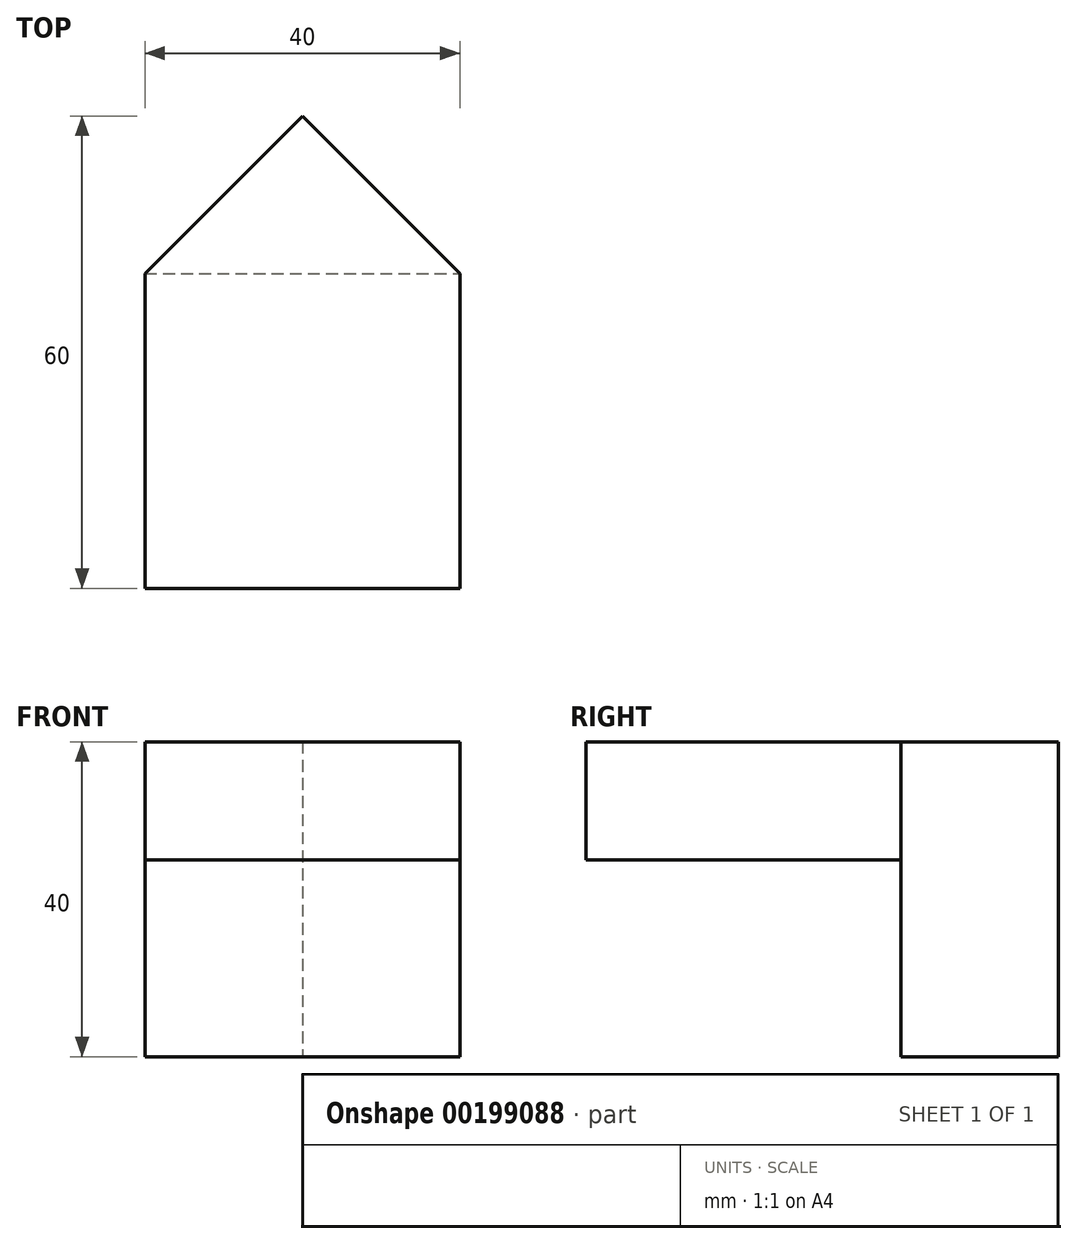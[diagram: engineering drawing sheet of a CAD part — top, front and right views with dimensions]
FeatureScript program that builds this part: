
annotation { "Feature Type Name" : "Feature", "Feature Type Description" : "" }
export const myFeature = defineFeature(function(context is Context, id is Id, definition is map)
    precondition{}
    {
        {
            var Q0;
            Q0=qCreatedBy(makeId("Top.planeOp"),FACE);
            var sketch = newSketch(context, id + "F0", { "sketchPlane" : qUnion([Q0])});
            skLineSegment(sketch, "E0.bottom", {"start": v(0, 0) * mm, "end": v(40, 0) * mm});
            skLineSegment(sketch, "E0.top", {"start": v(0, -40) * mm, "end": v(40, -40) * mm});
            skLineSegment(sketch, "E0.left", {"start": v(0, 0) * mm, "end": v(0, -40) * mm});
            skLineSegment(sketch, "E0.right", {"start": v(40, 0) * mm, "end": v(40, -40) * mm});
            skLineSegment(sketch, "E1", {"start": v(0, 0) * mm, "end": v(20, 20) * mm});
            skLineSegment(sketch, "E2", {"start": v(20, 20) * mm, "end": v(40, 0) * mm});
            skSolve(sketch);
        }
        {
            var Q0;
            Q0 = qSketchRegion(id + "F0", true);
            extrude(context, id + "F1", {"entities" : qUnion([Q0]), "depth" : 40 * mm, "offsetDistance" : 25 * mm});
        }
        {
            var Q0;
            Q0=makeQuery(id+"F0.imprint","IMPRINT",FACE,{"disambiguationData":[TD([[makeQuery(id+"F0.imprint","IMPRINT",EDGE,{"derivedFrom":sQuery(id+"F0.wireOp",EDGE,"E0.bottom")}),-1.0]])]});
            extrude(context, id + "F2", {"entities" : qUnion([Q0]), "operationType" : NewBodyOperationType.REMOVE, "depth" : 25 * mm, "offsetDistance" : 25 * mm});
        }
    });
